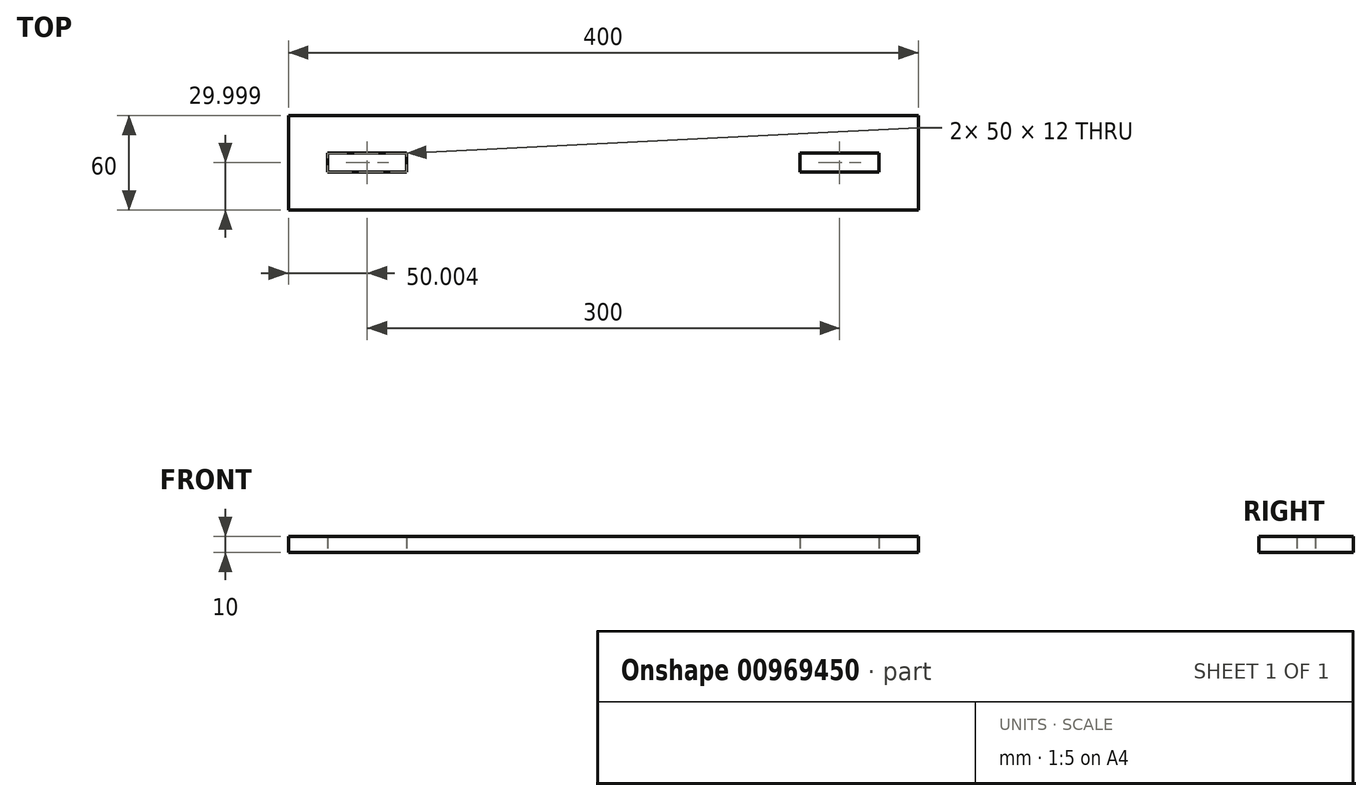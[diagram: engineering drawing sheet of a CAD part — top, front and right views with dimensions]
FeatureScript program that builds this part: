
annotation { "Feature Type Name" : "Feature", "Feature Type Description" : "" }
export const myFeature = defineFeature(function(context is Context, id is Id, definition is map)
    precondition{}
    {
        {
            var Q0;
            Q0=qCreatedBy(makeId("Top.planeOp"),FACE);
            var sketch = newSketch(context, id + "F0", { "sketchPlane" : qUnion([Q0])});
            skLineSegment(sketch, "E0.bottom", {"start": v(-190.65, -46.64) * mm, "end": v(209.35, -46.64) * mm});
            skLineSegment(sketch, "E0.top", {"start": v(-190.65, 13.36) * mm, "end": v(209.35, 13.36) * mm});
            skLineSegment(sketch, "E0.left", {"start": v(-190.65, -46.64) * mm, "end": v(-190.65, 13.36) * mm});
            skLineSegment(sketch, "E0.right", {"start": v(209.35, -46.64) * mm, "end": v(209.35, 13.36) * mm});
            skLineSegment(sketch, "E1.bottom", {"start": v(134.35, -22.64) * mm, "end": v(184.35, -22.64) * mm});
            skLineSegment(sketch, "E1.top", {"start": v(134.35, -10.64) * mm, "end": v(184.35, -10.64) * mm});
            skLineSegment(sketch, "E1.left", {"start": v(134.35, -22.64) * mm, "end": v(134.35, -10.64) * mm});
            skLineSegment(sketch, "E1.right", {"start": v(184.35, -22.64) * mm, "end": v(184.35, -10.64) * mm});
            skLineSegment(sketch, "E2.bottom", {"start": v(-165.65, -22.64) * mm, "end": v(-115.65, -22.64) * mm});
            skLineSegment(sketch, "E2.top", {"start": v(-165.65, -10.64) * mm, "end": v(-115.65, -10.64) * mm});
            skLineSegment(sketch, "E2.left", {"start": v(-165.65, -22.64) * mm, "end": v(-165.65, -10.64) * mm});
            skLineSegment(sketch, "E2.right", {"start": v(-115.65, -22.64) * mm, "end": v(-115.65, -10.64) * mm});
            skSolve(sketch);
        }
        {
            var Q0;
            Q0=makeQuery(id+"F0.imprint","IMPRINT",FACE,{"disambiguationData":[TD([[makeQuery(id+"F0.imprint","IMPRINT",EDGE,{"derivedFrom":sQuery(id+"F0.wireOp",EDGE,"E0.bottom")}),1.0]])]});
            extrude(context, id + "F1", {"entities" : qUnion([Q0]), "depth" : 10 * mm, "offsetDistance" : 25 * mm});
        }
    });
